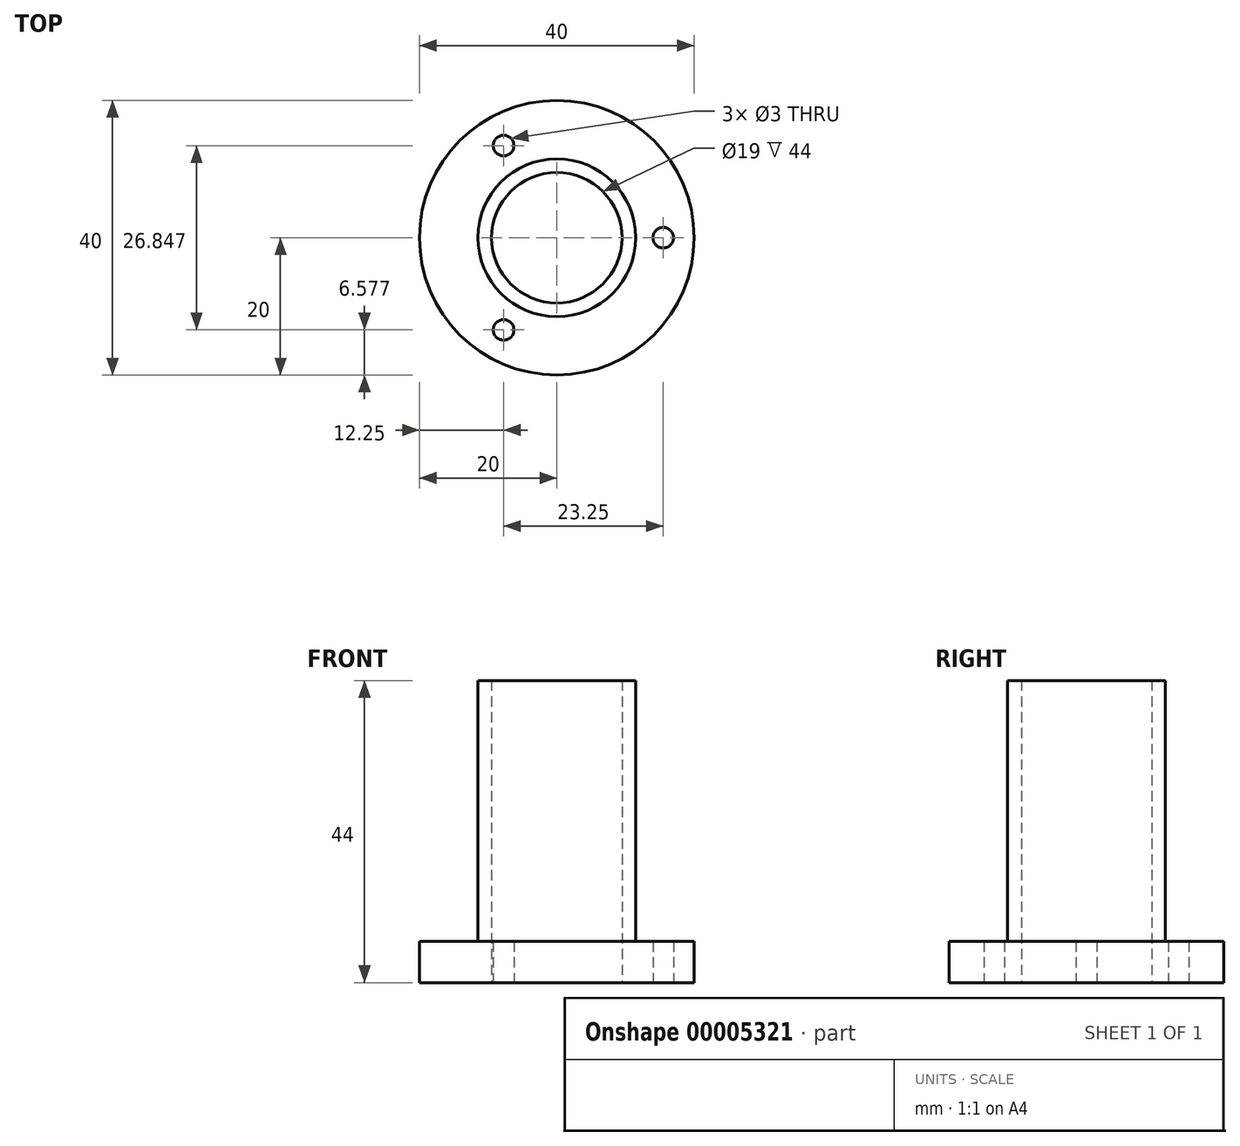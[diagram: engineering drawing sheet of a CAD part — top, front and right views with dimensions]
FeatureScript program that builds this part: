
annotation { "Feature Type Name" : "Feature", "Feature Type Description" : "" }
export const myFeature = defineFeature(function(context is Context, id is Id, definition is map)
    precondition{}
    {
        {
            var Q0;
            Q0=qCreatedBy(makeId("Top.planeOp"),FACE);
            var sketch = newSketch(context, id + "F0", { "sketchPlane" : qUnion([Q0])});
            skCircle(sketch, "E0", {"center": v(0, 0) * mm, "radius": 9.5 * mm});
            skCircle(sketch, "E1", {"center": v(0, 0) * mm, "radius": 11.5 * mm});
            skCircle(sketch, "E2", {"center": v(0, 0) * mm, "radius": 20 * mm});
            skCircle(sketch, "E3", {"center": v(15.5, 0) * mm, "radius": 1.5 * mm});
            skCircle(sketch, "E4.1.0", {"center": v(-7.75, 13.42) * mm, "radius": 1.5 * mm});
            skCircle(sketch, "E4.2.0", {"center": v(-7.75, -13.42) * mm, "radius": 1.5 * mm});
            skSolve(sketch);
        }
        {
            var Q0;
            Q0=makeQuery(id+"F0.imprint","IMPRINT",FACE,{"disambiguationData":[TD([[makeQuery(id+"F0.imprint","IMPRINT",EDGE,{"derivedFrom":sQuery(id+"F0.wireOp",EDGE,"E1")}),-1.0]])]});
            extrude(context, id + "F1", {"entities" : qUnion([Q0]), "depth" : 6 * mm});
        }
        {
            var Q0;
            Q0=makeQuery(id+"F0.imprint","IMPRINT",FACE,{"disambiguationData":[TD([[makeQuery(id+"F0.imprint","IMPRINT",EDGE,{"derivedFrom":sQuery(id+"F0.wireOp",EDGE,"E0")}),-1.0]])]});
            var Q1;
            Q1=sQuery(id+"F0.wireOp",EDGE,"E0");
            var Q2;
            Q2=sQuery(id+"F0.wireOp",EDGE,"E1");
            extrude(context, id + "F2", {"entities" : qUnion([Q0]), "operationType" : NewBodyOperationType.ADD, "surfaceEntities" : qUnion([Q1, Q2]), "depth" : 44 * mm});
        }
    });
